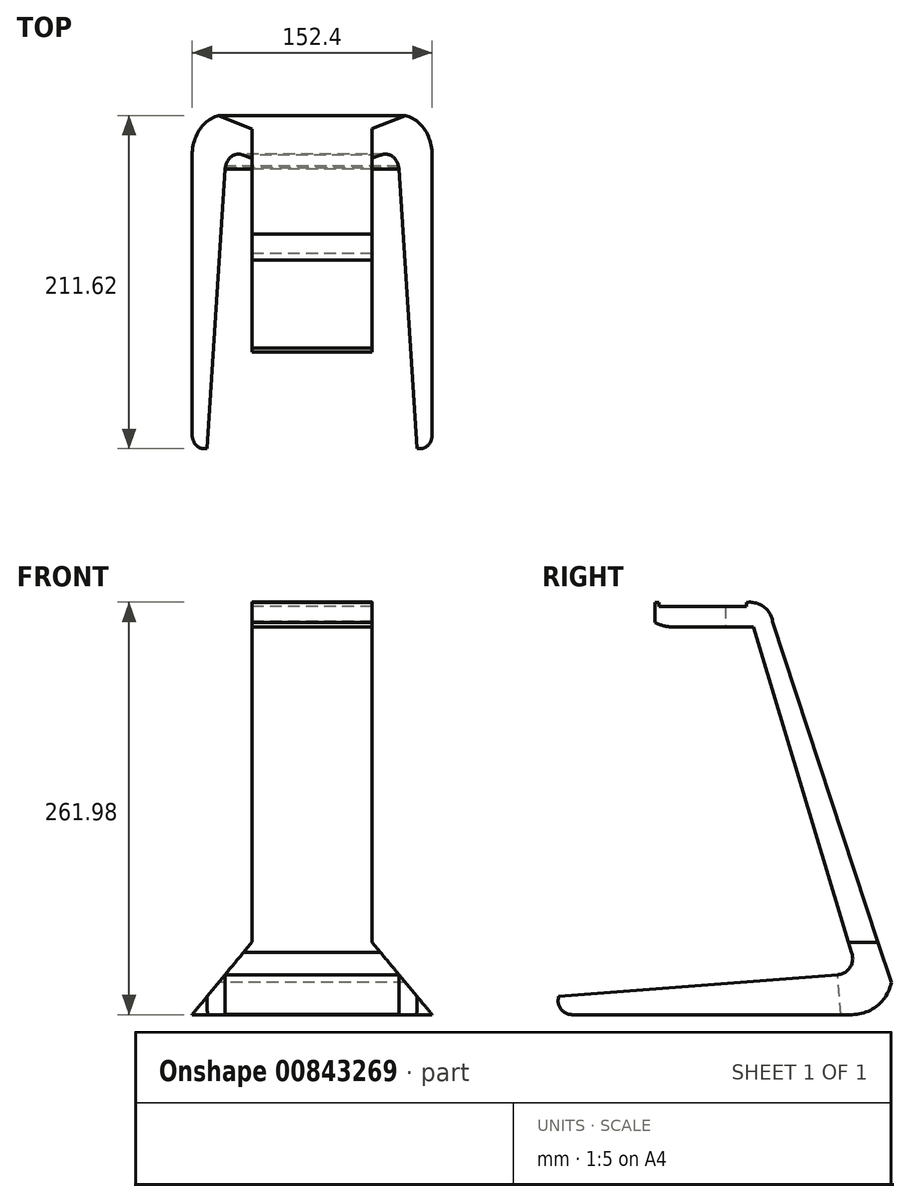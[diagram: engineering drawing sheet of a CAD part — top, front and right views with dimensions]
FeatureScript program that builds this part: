
annotation { "Feature Type Name" : "Feature", "Feature Type Description" : "" }
export const myFeature = defineFeature(function(context is Context, id is Id, definition is map)
    precondition{}
    {
        {
            var Q0;
            Q0=qCreatedBy(makeId("Right.planeOp"),FACE);
            var sketch = newSketch(context, id + "F0", { "sketchPlane" : qUnion([Q0])});
            skLineSegment(sketch, "E0", {"start": v(-97.43, -122.43) * mm, "end": v(80.37, -122.43) * mm});
            skArc(sketch, "E1", {"start": v(80.37, -122.43) * mm, "mid": v(96.51, -116.64) * mm, "end": v(105.3, -101.92) * mm});
            skArc(sketch, "E2", {"start": v(-105.93, -110.92) * mm, "mid": v(-104.58, -118.82) * mm, "end": v(-97.43, -122.43) * mm});
            skLineSegment(sketch, "E3", {"start": v(-105.93, -110.92) * mm, "end": v(71.33, -97.03) * mm});
            skArc(sketch, "E4", {"start": v(71.33, -97.03) * mm, "mid": v(79.3, -92.14) * mm, "end": v(80.02, -82.81) * mm});
            skLineSegment(sketch, "E5", {"start": v(80.02, -82.81) * mm, "end": v(17.62, 123.88) * mm});
            skLineSegment(sketch, "E6", {"start": v(17.62, 123.88) * mm, "end": v(-33.18, 123.88) * mm});
            skArc(sketch, "E7", {"start": v(-44.85, 126.72) * mm, "mid": v(-39.18, 124.6) * mm, "end": v(-33.18, 123.88) * mm});
            skLineSegment(sketch, "E8", {"start": v(-44.85, 139.42) * mm, "end": v(-44.85, 126.72) * mm});
            skArc(sketch, "E9", {"start": v(29.95, 127.32) * mm, "mid": v(24.22, 136.7) * mm, "end": v(13.57, 139.42) * mm});
            skLineSegment(sketch, "E10", {"start": v(-44.85, 139.42) * mm, "end": v(13.57, 139.42) * mm});
            skLineSegment(sketch, "E11", {"start": v(29.95, 127.32) * mm, "end": v(105.3, -101.92) * mm});
            skSolve(sketch);
        }
        {
            var Q0;
            Q0 = qSketchRegion(id + "F0", true);
            extrude(context, id + "F1", {"entities" : qUnion([Q0]), "endBound" : BoundingType.SYMMETRIC, "depth" : 152.4 * mm, "offsetDistance" : 25.4 * mm});
        }
        {
            var Q0;
            Q0=qCreatedBy(makeId("Front.planeOp"),FACE);
            var sketch = newSketch(context, id + "F2", { "sketchPlane" : qUnion([Q0])});
            skPoint(sketch, "E12", {"position": v(0, 139.42) * mm});
            skLineSegment(sketch, "E13", {"start": v(0, 139.42) * mm, "end": v(-76.2, 139.42) * mm});
            skLineSegment(sketch, "E14", {"start": v(0, 139.42) * mm, "end": v(76.2, 139.42) * mm});
            skLineSegment(sketch, "E15", {"start": v(-38.1, 139.42) * mm, "end": v(-38.1, -76.2) * mm});
            skLineSegment(sketch, "E16", {"start": v(38.1, 139.42) * mm, "end": v(38.1, -76.55) * mm});
            skLineSegment(sketch, "E17", {"start": v(-76.2, 139.42) * mm, "end": v(-76.2, -76.2) * mm});
            skLineSegment(sketch, "E18", {"start": v(-76.2, -76.2) * mm, "end": v(-38.1, -76.2) * mm});
            skLineSegment(sketch, "E19", {"start": v(76.2, 139.42) * mm, "end": v(76.2, -76.55) * mm});
            skLineSegment(sketch, "E20", {"start": v(76.2, -76.55) * mm, "end": v(38.1, -76.55) * mm});
            skSolve(sketch);
        }
        {
            var Q0;
            Q0 = qSketchRegion(id + "F2", true);
            extrude(context, id + "F3", {"entities" : qUnion([Q0]), "operationType" : NewBodyOperationType.REMOVE, "oppositeDirection" : true, "depth" : 247.9 * mm, "offsetDistance" : 25.4 * mm});
        }
        {
            var Q0;
            Q0=qCreatedBy(makeId("Front.planeOp"),FACE);
            var sketch = newSketch(context, id + "F4", { "sketchPlane" : qUnion([Q0])});
            skLineSegment(sketch, "E21", {"start": v(-38.11, 139.58) * mm, "end": v(-38.11, 123.88) * mm});
            skLineSegment(sketch, "E22", {"start": v(-38.11, 123.88) * mm, "end": v(-77.09, 123.88) * mm});
            skLineSegment(sketch, "E23", {"start": v(-77.09, 123.88) * mm, "end": v(-77.09, 139.58) * mm});
            skLineSegment(sketch, "E24", {"start": v(-77.09, 139.58) * mm, "end": v(-38.11, 139.58) * mm});
            skSolve(sketch);
        }
        {
            var Q0;
            Q0 = qSketchRegion(id + "F4", true);
            extrude(context, id + "F5", {"entities" : qUnion([Q0]), "operationType" : NewBodyOperationType.REMOVE, "depth" : 129.03 * mm, "offsetDistance" : 25.4 * mm});
        }
        {
            var Q0;
            Q0=makeQuery(id+"F3.boolean.opBoolean","COPY",FACE,{"derivedFrom":makeQuery(id+"F3.opExtrude","CAP_FACE",FACE,{"disambiguationData":[OSD([sQuery(id+"F2.wireOp",EDGE,"E14"),sQuery(id+"F2.wireOp",EDGE,"E16"),sQuery(id+"F2.wireOp",EDGE,"E19"),sQuery(id+"F2.wireOp",EDGE,"E20")])],"isStart":true})});
            var sketch = newSketch(context, id + "F6", { "sketchPlane" : qUnion([Q0])});
            skLineSegment(sketch, "E25", {"start": v(-38.1, 123.88) * mm, "end": v(-38.1, 139.42) * mm});
            skLineSegment(sketch, "E26", {"start": v(-38.1, 139.42) * mm, "end": v(-76.2, 139.42) * mm});
            skLineSegment(sketch, "E27", {"start": v(-76.2, 139.42) * mm, "end": v(-76.2, 123.88) * mm});
            skLineSegment(sketch, "E28", {"start": v(-76.2, 123.88) * mm, "end": v(-38.1, 123.88) * mm});
            skSolve(sketch);
        }
        {
            var Q0;
            Q0 = qSketchRegion(id + "F6", true);
            extrude(context, id + "F7", {"entities" : qUnion([Q0]), "operationType" : NewBodyOperationType.REMOVE, "oppositeDirection" : true, "depth" : 71.63 * mm, "offsetDistance" : 25.4 * mm});
        }
        {
            var Q0;
            Q0=qCreatedBy(makeId("Top.planeOp"),FACE);
            var sketch = newSketch(context, id + "F8", { "sketchPlane" : qUnion([Q0])});
            skLineSegment(sketch, "E29", {"start": v(-38.1, 13.57) * mm, "end": v(-38.1, 17.51) * mm});
            skLineSegment(sketch, "E30", {"start": v(-38.1, 17.51) * mm, "end": v(-77.63, 17.51) * mm});
            skLineSegment(sketch, "E31", {"start": v(-77.63, 17.51) * mm, "end": v(-77.63, 13.57) * mm});
            skLineSegment(sketch, "E32", {"start": v(-77.63, 13.57) * mm, "end": v(-38.1, 13.57) * mm});
            skSolve(sketch);
        }
        {
            var Q0;
            Q0 = qSketchRegion(id + "F8", true);
            extrude(context, id + "F9", {"entities" : qUnion([Q0]), "operationType" : NewBodyOperationType.REMOVE, "depth" : 211.33 * mm, "offsetDistance" : 25.4 * mm});
        }
        {
            var Q0;
            Q0=qCreatedBy(makeId("Top.planeOp"),FACE);
            var sketch = newSketch(context, id + "F10", { "sketchPlane" : qUnion([Q0])});
            skLineSegment(sketch, "E33.bottom", {"start": v(38.1, 17.51) * mm, "end": v(113.11, 17.51) * mm});
            skLineSegment(sketch, "E33.top", {"start": v(38.1, 11.28) * mm, "end": v(113.11, 11.28) * mm});
            skLineSegment(sketch, "E33.left", {"start": v(38.1, 17.51) * mm, "end": v(38.1, 11.28) * mm});
            skLineSegment(sketch, "E33.right", {"start": v(113.11, 17.51) * mm, "end": v(113.11, 11.28) * mm});
            skSolve(sketch);
        }
        {
            var Q0;
            Q0 = qSketchRegion(id + "F10", true);
            extrude(context, id + "F11", {"entities" : qUnion([Q0]), "operationType" : NewBodyOperationType.REMOVE, "depth" : 846.84 * mm, "offsetDistance" : 25.4 * mm});
        }
        {
            var Q0;
            Q0=qCreatedBy(makeId("Front.planeOp"),FACE);
            var sketch = newSketch(context, id + "F12", { "sketchPlane" : qUnion([Q0])});
            skLineSegment(sketch, "E34", {"start": v(-38.1, -76.2) * mm, "end": v(-76.2, -122.43) * mm});
            skLineSegment(sketch, "E35", {"start": v(-76.2, -122.43) * mm, "end": v(-76.2, -76.2) * mm});
            skLineSegment(sketch, "E36", {"start": v(-76.2, -76.2) * mm, "end": v(-38.1, -76.2) * mm});
            skSolve(sketch);
        }
        {
            var Q0;
            Q0 = qSketchRegion(id + "F12", true);
            extrude(context, id + "F13", {"entities" : qUnion([Q0]), "operationType" : NewBodyOperationType.REMOVE, "endBound" : BoundingType.SYMMETRIC, "depth" : 666 * mm, "offsetDistance" : 25.4 * mm});
        }
        {
            var Q0;
            Q0=qCreatedBy(makeId("Front.planeOp"),FACE);
            var sketch = newSketch(context, id + "F14", { "sketchPlane" : qUnion([Q0])});
            skLineSegment(sketch, "E37", {"start": v(38.1, -76.55) * mm, "end": v(76.2, -122.43) * mm});
            skLineSegment(sketch, "E38", {"start": v(76.2, -122.43) * mm, "end": v(76.2, -76.55) * mm});
            skLineSegment(sketch, "E39", {"start": v(76.2, -76.55) * mm, "end": v(38.1, -76.55) * mm});
            skSolve(sketch);
        }
        {
            var Q0;
            Q0 = qSketchRegion(id + "F14", true);
            extrude(context, id + "F15", {"entities" : qUnion([Q0]), "operationType" : NewBodyOperationType.REMOVE, "endBound" : BoundingType.SYMMETRIC, "oppositeDirection" : true, "depth" : 654.8 * mm, "offsetDistance" : 25.4 * mm});
        }
        {
            var Q0;
            Q0=qCreatedBy(makeId("Right.planeOp"),FACE);
            var sketch = newSketch(context, id + "F16", { "sketchPlane" : qUnion([Q0])});
            skLineSegment(sketch, "E40.bottom", {"start": v(13.37, 145.42) * mm, "end": v(-42.26, 145.42) * mm});
            skLineSegment(sketch, "E40.top", {"start": v(13.37, 136.7) * mm, "end": v(-42.26, 136.7) * mm});
            skLineSegment(sketch, "E40.left", {"start": v(13.37, 145.42) * mm, "end": v(13.37, 136.7) * mm});
            skLineSegment(sketch, "E40.right", {"start": v(-42.26, 145.42) * mm, "end": v(-42.26, 136.7) * mm});
            skSolve(sketch);
        }
        {
            var Q0;
            Q0 = qSketchRegion(id + "F16", true);
            extrude(context, id + "F17", {"entities" : qUnion([Q0]), "operationType" : NewBodyOperationType.REMOVE, "endBound" : BoundingType.SYMMETRIC, "depth" : 109.98 * mm, "offsetDistance" : 25.4 * mm});
        }
        {
            var Q0;
            Q0=makeQuery(id+"F1.opExtrude","SWEPT_FACE",FACE,{"disambiguationData":[OSD([sQuery(id+"F0.wireOp",EDGE,"E3")])]});
            var sketch = newSketch(context, id + "F18", { "sketchPlane" : qUnion([Q0])});
            skLineSegment(sketch, "E41", {"start": v(-55.27, 63.53) * mm, "end": v(-66.72, -114.27) * mm});
            skLineSegment(sketch, "E42", {"start": v(-66.72, -114.27) * mm, "end": v(66.64, -114.27) * mm});
            skLineSegment(sketch, "E43", {"start": v(66.64, -114.27) * mm, "end": v(55.1, 63.53) * mm});
            skLineSegment(sketch, "E44", {"start": v(55.1, 63.53) * mm, "end": v(-55.27, 63.53) * mm});
            skSolve(sketch);
        }
        {
            var Q0;
            Q0 = qSketchRegion(id + "F18", true);
            extrude(context, id + "F19", {"entities" : qUnion([Q0]), "operationType" : NewBodyOperationType.REMOVE, "oppositeDirection" : true, "depth" : 25.4 * mm, "offsetDistance" : 25.4 * mm});
        }
        {
            var Q0;
            Q0=qCreatedBy(makeId("Top.planeOp"),FACE);
            var sketch = newSketch(context, id + "F20", { "sketchPlane" : qUnion([Q0])});
            skLineSegment(sketch, "E45.bottom", {"start": v(66.61, -105.41) * mm, "end": v(-66.68, -105.41) * mm});
            skLineSegment(sketch, "E45.top", {"start": v(66.61, -106.49) * mm, "end": v(-66.68, -106.49) * mm});
            skLineSegment(sketch, "E45.left", {"start": v(66.61, -105.41) * mm, "end": v(66.61, -106.49) * mm});
            skLineSegment(sketch, "E45.right", {"start": v(-66.68, -105.41) * mm, "end": v(-66.68, -106.49) * mm});
            skSolve(sketch);
        }
        {
            var Q0;
            Q0 = qSketchRegion(id + "F20", true);
            extrude(context, id + "F21", {"entities" : qUnion([Q0]), "operationType" : NewBodyOperationType.REMOVE, "oppositeDirection" : true, "depth" : 231.9 * mm, "offsetDistance" : 25.4 * mm});
        }
    });
